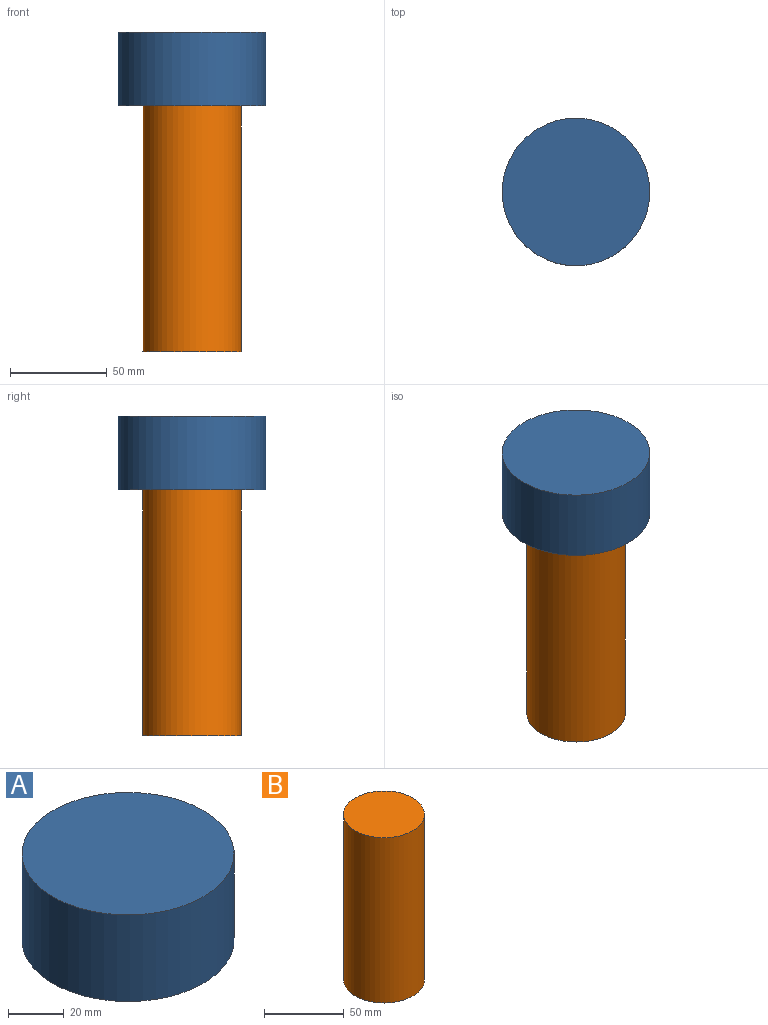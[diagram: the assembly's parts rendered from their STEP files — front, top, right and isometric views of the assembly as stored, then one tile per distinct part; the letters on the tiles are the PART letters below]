
ASSEMBLY  parts=2 mates=1
PART A: 3 faces, bbox 76.2x76.2x38.1 mm
  f0: cylinder r=38.1mm len=76.2mm, axis (0,0,-1), area 9120.7mm2, adj f1,f2
  f1: plane 76.2x76.2mm, normal (0,0,1), area 4560.4mm2, adj f0
  f2: plane 76.2x76.2mm, normal (0,0,-1), area 4560.4mm2, adj f0
PART B: 3 faces, bbox 50.8x50.8x127 mm
  f0: cylinder r=25.4mm len=127mm, axis (0,0,-1), area 20268.3mm2, adj f1,f2
  f1: plane 50.8x50.8mm, normal (0,0,1), area 2026.8mm2, adj f0
  f2: plane 50.8x50.8mm, normal (0,0,-1), area 2026.8mm2, adj f0
PLACE A t=(-66.27,-2.25,117.51)mm
PLACE B t=(-66.27,-2.25,-9.49)mm
MATE revolute A.f0 <-> B.f0  axis (0,0,-1) through (-66.27,-2.25,117.51)mm
